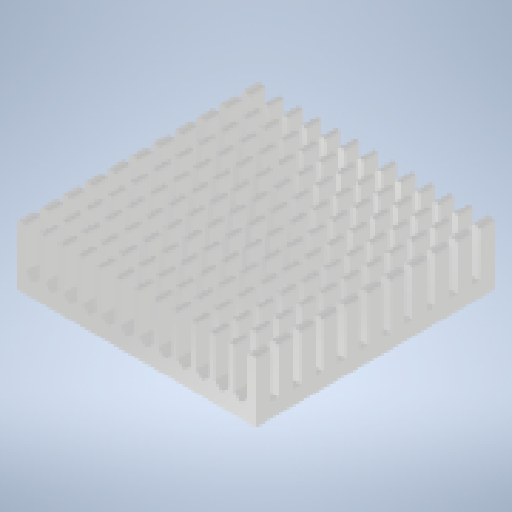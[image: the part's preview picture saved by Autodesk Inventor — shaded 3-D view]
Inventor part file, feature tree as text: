
AUTODESK INVENTOR PART (.ipt)
format: ipt  version: 2023.1 (Build 271208000, 208)  size: 988,160 bytes
history: native  units: mm
features: other x3, move_body x3, sketch x2, extrude x2, projected_geometry x2, plane x1, chamfer x1, direct_edit x1, fillet x1, reference x1
ambient origin geometry x8: Origin, YZ Plane, XZ Plane, XY Plane, X Axis, Y Axis, Z Axis, Center Point
bodies: Volumenkörper1 (feature_tree)
feature tree (17):
  sketch  "Skizze1"  dims[d0=0.8mm d1=10.0mm d2=0.0mm d3=0.5mm d4=2.0mm d5=45.0deg]
  plane  "Arbeitsebene1"
  extrude  "Extrusion1"  Depth=10.0mm TaperAngle=0.0deg
  chamfer  "Fase1"  Distance=0.5mm Angle=45.0deg
  direct_edit  "Direktbearbeitung1"
  fillet  "Rundung1"  [1 undecoded]
  extrude  "Extrusion2"  TaperAngle=0.0deg  [1 undecoded]
  reference  "Referenz1"
  sketch  "Skizze2"  dims[d6=0.0mm d7=0.0mm d8=6.0mm d9=0.0mm d10=0.0mm d11=-0.5mm d12=0.0mm d13=0.0mm d14=-0.5mm d15=0.5mm d16=2.5mm d17=2.5mm d18=2.5mm d19=2.5mm d20=2.5mm d21=2.5mm d22=2.5mm d23=2.5mm d24=2.5mm d25=2.5mm d26=2.5mm d27=1.29mm d28=1.29mm d29=1.29mm d30=1.29mm d31=1.29mm d32=1.29mm d33=1.29mm d34=1.29mm d35=1.29mm d36=1.29mm d37=0.0mm d38=0.0mm]
  projected_geometry  "Projizierte Kontur1"
  projected_geometry  "Projizierte Kontur2"
  other  "<userpath>\Desktop\GitHub\Voron-2-Mods\Arducam_IMX477_CM4\CM4\CAD\Source\CM4_Case.iam"
  other  "CM4_Case.iam"
  other  "CM4_Case_Buttom:1"
  move_body  "Verschieben1"
  move_body  "Verschieben2"
  move_body  "Verschieben3"
note: 2 required parameter values undecoded (feature->parameter linkage not recoverable at this tier; creation-order binding heuristic only, values carry confidence <= 0.55)
